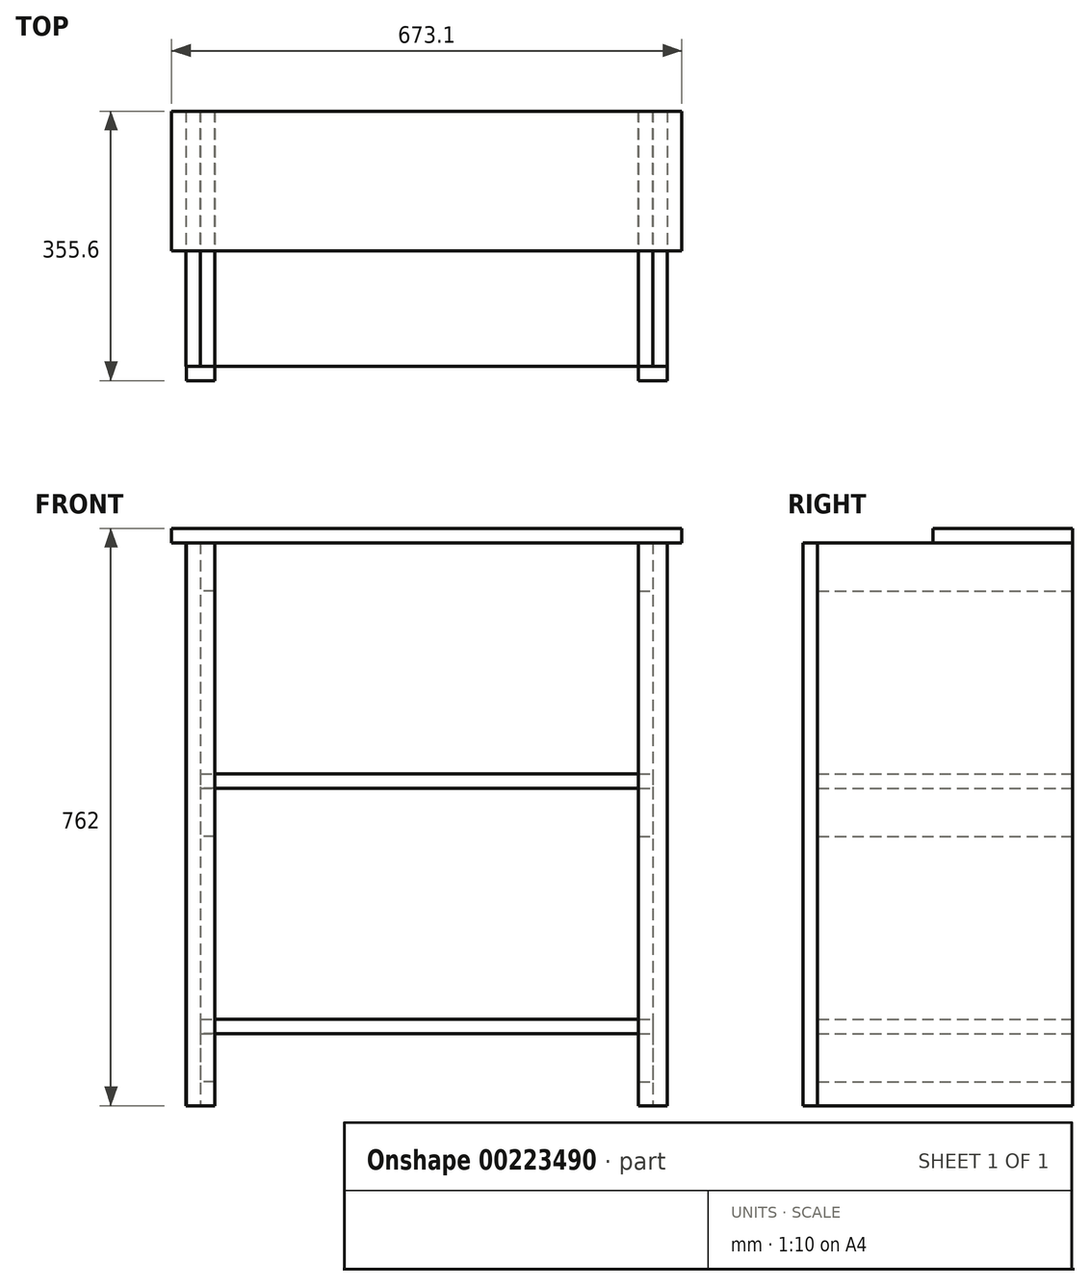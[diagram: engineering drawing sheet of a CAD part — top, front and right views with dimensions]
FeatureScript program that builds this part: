
annotation { "Feature Type Name" : "Feature", "Feature Type Description" : "" }
export const myFeature = defineFeature(function(context is Context, id is Id, definition is map)
    precondition{}
    {
        {
            var Q0;
            Q0=qCreatedBy(makeId("Top.planeOp"),FACE);
            var sketch = newSketch(context, id + "F0", { "sketchPlane" : qUnion([Q0])});
            skLineSegment(sketch, "E0.bottom", {"start": v(-59.58, 81.02) * mm, "end": v(-40.53, 81.02) * mm});
            skLineSegment(sketch, "E0.top", {"start": v(-59.58, 17.52) * mm, "end": v(-40.53, 17.52) * mm});
            skLineSegment(sketch, "E0.left", {"start": v(-59.58, 81.02) * mm, "end": v(-59.58, 17.52) * mm});
            skLineSegment(sketch, "E0.right", {"start": v(-40.53, 81.02) * mm, "end": v(-40.53, 17.52) * mm});
            skLineSegment(sketch, "E1.bottom", {"start": v(-59.58, -192.03) * mm, "end": v(-40.53, -192.03) * mm});
            skLineSegment(sketch, "E1.top", {"start": v(-59.58, -255.53) * mm, "end": v(-40.53, -255.53) * mm});
            skLineSegment(sketch, "E1.left", {"start": v(-59.58, -192.03) * mm, "end": v(-59.58, -255.53) * mm});
            skLineSegment(sketch, "E1.right", {"start": v(-40.53, -192.03) * mm, "end": v(-40.53, -255.53) * mm});
            skLineSegment(sketch, "E2", {"start": v(257.92, 81.02) * mm, "end": v(257.92, -255.53) * mm});
            skLineSegment(sketch, "E3.MirrorCS", {"start": v(575.42, -192.03) * mm, "end": v(575.42, -255.53) * mm});
            skLineSegment(sketch, "E4.MirrorCS", {"start": v(556.37, -192.03) * mm, "end": v(556.37, -255.53) * mm});
            skLineSegment(sketch, "E5.MirrorCS", {"start": v(575.42, -192.03) * mm, "end": v(556.37, -192.03) * mm});
            skLineSegment(sketch, "E6.MirrorCS", {"start": v(575.42, -255.53) * mm, "end": v(556.37, -255.53) * mm});
            skLineSegment(sketch, "E7.MirrorCS", {"start": v(575.42, 17.52) * mm, "end": v(556.37, 17.52) * mm});
            skLineSegment(sketch, "E8.MirrorCS", {"start": v(575.42, 81.02) * mm, "end": v(575.42, 17.52) * mm});
            skLineSegment(sketch, "E9.MirrorCS", {"start": v(556.37, 81.02) * mm, "end": v(556.37, 17.52) * mm});
            skLineSegment(sketch, "E10.MirrorCS", {"start": v(575.42, 81.02) * mm, "end": v(556.37, 81.02) * mm});
            skSolve(sketch);
        }
        {
            var Q0;
            Q0=makeQuery(id+"F0.imprint","IMPRINT",FACE,{"disambiguationData":[TD([[makeQuery(id+"F0.imprint","IMPRINT",EDGE,{"derivedFrom":sQuery(id+"F0.wireOp",EDGE,"E0.bottom")}),-1.0]])]});
            var Q1;
            Q1=makeQuery(id+"F0.imprint","IMPRINT",FACE,{"disambiguationData":[TD([[makeQuery(id+"F0.imprint","IMPRINT",EDGE,{"derivedFrom":sQuery(id+"F0.wireOp",EDGE,"E1.bottom")}),-1.0]])]});
            var Q2;
            Q2=makeQuery(id+"F0.imprint","IMPRINT",FACE,{"disambiguationData":[TD([[makeQuery(id+"F0.imprint","IMPRINT",EDGE,{"derivedFrom":sQuery(id+"F0.wireOp",EDGE,"E3.MirrorCS")}),-1.0]])]});
            var Q3;
            Q3=makeQuery(id+"F0.imprint","IMPRINT",FACE,{"disambiguationData":[TD([[makeQuery(id+"F0.imprint","IMPRINT",EDGE,{"derivedFrom":sQuery(id+"F0.wireOp",EDGE,"E7.MirrorCS")}),-1.0]])]});
            extrude(context, id + "F1", {"entities" : qUnion([Q0, Q1, Q2, Q3]), "depth" : 742.95 * mm});
        }
        {
            var Q0;
            Q0=makeQuery(id+"F1.opExtrude","CAP_FACE",FACE,{"disambiguationData":[OSD([sQuery(id+"F0.wireOp",EDGE,"E7.MirrorCS"),sQuery(id+"F0.wireOp",EDGE,"E8.MirrorCS"),sQuery(id+"F0.wireOp",EDGE,"E9.MirrorCS"),sQuery(id+"F0.wireOp",EDGE,"E10.MirrorCS")])],"isStart":false});
            var sketch = newSketch(context, id + "F2", { "sketchPlane" : qUnion([Q0])});
            skLineSegment(sketch, "E11.bottom", {"start": v(594.47, 81.02) * mm, "end": v(-78.63, 81.02) * mm});
            skLineSegment(sketch, "E11.top", {"start": v(594.47, -103.13) * mm, "end": v(-78.63, -103.13) * mm});
            skLineSegment(sketch, "E11.left", {"start": v(594.47, 81.02) * mm, "end": v(594.47, -103.13) * mm});
            skLineSegment(sketch, "E11.right", {"start": v(-78.63, 81.02) * mm, "end": v(-78.63, -103.13) * mm});
            skLineSegment(sketch, "E12.bottom", {"start": v(-78.63, -103.13) * mm, "end": v(594.47, -103.13) * mm});
            skLineSegment(sketch, "E12.top", {"start": v(-78.63, -282.2) * mm, "end": v(594.47, -282.2) * mm});
            skLineSegment(sketch, "E12.left", {"start": v(-78.63, -103.13) * mm, "end": v(-78.63, -282.2) * mm});
            skLineSegment(sketch, "E12.right", {"start": v(594.47, -103.13) * mm, "end": v(594.47, -282.2) * mm});
            skSolve(sketch);
        }
        {
            var Q0;
            Q0=makeQuery(id+"F2.imprint","IMPRINT",FACE,{"disambiguationData":[TD([[makeQuery(id+"F2.imprint","IMPRINT",EDGE,{"derivedFrom":makeQuery(id+"F1.opExtrude","CAP_EDGE",EDGE,{"disambiguationData":[OSD([sQuery(id+"F0.wireOp",EDGE,"E7.MirrorCS")])],"isStart":false})}),-1.0]])]});
            var Q1;
            {var subQ2=sQuery(id+"F2.wireOp",EDGE,"E11.left");Q1=makeQuery(id+"F2.imprint","IMPRINT",FACE,{"disambiguationData":[TD([[makeQuery(id+"F2.imprint","IMPRINT",EDGE,{"derivedFrom":subQ2}),-1.0]])]});}
            var Q2;
            Q2=makeQuery(id+"F2.imprint","IMPRINT",FACE,{"disambiguationData":[TD([[makeQuery(id+"F2.imprint","IMPRINT",EDGE,{"derivedFrom":sQuery(id+"F2.wireOp",EDGE,"E12.bottom")}),-1.0]])]});
            extrude(context, id + "F3", {"entities" : qUnion([Q0, Q1, Q2]), "depth" : 19.05 * mm});
        }
        {
            var Q0;
            Q0=makeQuery(id+"F1.opExtrude","SWEPT_FACE",FACE,{"disambiguationData":[OSD([sQuery(id+"F0.wireOp",EDGE,"E1.right")])]});
            var sketch = newSketch(context, id + "F4", { "sketchPlane" : qUnion([Q0])});
            skLineSegment(sketch, "E13.bottom", {"start": v(-255.53, 742.95) * mm, "end": v(81.02, 742.95) * mm});
            skLineSegment(sketch, "E13.top", {"start": v(-255.53, 679.45) * mm, "end": v(81.02, 679.45) * mm});
            skLineSegment(sketch, "E13.left", {"start": v(-255.53, 742.95) * mm, "end": v(-255.53, 679.45) * mm});
            skLineSegment(sketch, "E13.right", {"start": v(81.02, 742.95) * mm, "end": v(81.02, 679.45) * mm});
            skLineSegment(sketch, "E14.bottom", {"start": v(-255.53, 419.1) * mm, "end": v(81.02, 419.1) * mm});
            skLineSegment(sketch, "E14.top", {"start": v(-255.53, 355.6) * mm, "end": v(81.02, 355.6) * mm});
            skLineSegment(sketch, "E14.left", {"start": v(-255.53, 419.1) * mm, "end": v(-255.53, 355.6) * mm});
            skLineSegment(sketch, "E14.right", {"start": v(81.02, 419.1) * mm, "end": v(81.02, 355.6) * mm});
            skLineSegment(sketch, "E15.bottom", {"start": v(-255.53, 31.75) * mm, "end": v(81.02, 31.75) * mm});
            skLineSegment(sketch, "E15.top", {"start": v(-255.53, 95.25) * mm, "end": v(81.02, 95.25) * mm});
            skLineSegment(sketch, "E15.left", {"start": v(-255.53, 31.75) * mm, "end": v(-255.53, 95.25) * mm});
            skLineSegment(sketch, "E15.right", {"start": v(81.02, 31.75) * mm, "end": v(81.02, 95.25) * mm});
            skSolve(sketch);
        }
        {
            var Q0;
            {var subQ4=sQuery(id+"F4.wireOp",EDGE,"E13.left");Q0=makeQuery(id+"F4.imprint","IMPRINT",FACE,{"disambiguationData":[TD([[makeQuery(id+"F4.imprint","IMPRINT",EDGE,{"derivedFrom":subQ4}),1.0]])]});}
            var Q1;
            {var subQ3=sQuery(id+"F4.wireOp",EDGE,"E13.right");Q1=makeQuery(id+"F4.imprint","IMPRINT",FACE,{"disambiguationData":[TD([[makeQuery(id+"F4.imprint","IMPRINT",EDGE,{"derivedFrom":subQ3}),-1.0]])]});}
            var Q2;
            {var subQ0=sQuery(id+"F4.wireOp",EDGE,"E14.left");Q2=makeQuery(id+"F4.imprint","IMPRINT",FACE,{"disambiguationData":[TD([[makeQuery(id+"F4.imprint","IMPRINT",EDGE,{"derivedFrom":subQ0}),1.0]])]});}
            var Q3;
            {var subQ0=sQuery(id+"F4.wireOp",EDGE,"E14.right");Q3=makeQuery(id+"F4.imprint","IMPRINT",FACE,{"disambiguationData":[TD([[makeQuery(id+"F4.imprint","IMPRINT",EDGE,{"derivedFrom":subQ0}),-1.0]])]});}
            var Q4;
            {var subQ0=sQuery(id+"F4.wireOp",EDGE,"E15.left");Q4=makeQuery(id+"F4.imprint","IMPRINT",FACE,{"disambiguationData":[TD([[makeQuery(id+"F4.imprint","IMPRINT",EDGE,{"derivedFrom":subQ0}),1.0]])]});}
            var Q5;
            {var subQ0=sQuery(id+"F4.wireOp",EDGE,"E15.right");Q5=makeQuery(id+"F4.imprint","IMPRINT",FACE,{"disambiguationData":[TD([[makeQuery(id+"F4.imprint","IMPRINT",EDGE,{"derivedFrom":subQ0}),1.0]])]});}
            extrude(context, id + "F5", {"entities" : qUnion([Q0, Q1, Q2, Q3, Q4, Q5]), "depth" : 19.05 * mm});
        }
        {
            var Q0;
            Q0=makeQuery(id+"F1.opExtrude","SWEPT_FACE",FACE,{"disambiguationData":[OSD([sQuery(id+"F0.wireOp",EDGE,"E9.MirrorCS")])]});
            cPlane(context, id + "F6", {"entities" : qUnion([Q0]), "cplaneType" : CPlaneType.OFFSET, "offset" : 298.45 * mm, "width" : 152.4 * mm, "height" : 152.4 * mm});
        }
        {
            var Q0;
            Q0=makeQuery(id+"F5.opExtrude","SWEPT_BODY",BODY,{"disambiguationData":[OSD([sQuery(id+"F4.wireOp",EDGE,"E15.bottom"),sQuery(id+"F4.wireOp",EDGE,"E15.top"),sQuery(id+"F4.wireOp",EDGE,"E15.left"),sQuery(id+"F4.wireOp",EDGE,"E15.right")])]});
            var Q1;
            Q1=makeQuery(id+"F5.opExtrude","SWEPT_BODY",BODY,{"disambiguationData":[OSD([sQuery(id+"F4.wireOp",EDGE,"E14.bottom"),sQuery(id+"F4.wireOp",EDGE,"E14.top"),sQuery(id+"F4.wireOp",EDGE,"E14.left"),sQuery(id+"F4.wireOp",EDGE,"E14.right")])]});
            var Q2;
            Q2=makeQuery(id+"F5.opExtrude","SWEPT_BODY",BODY,{"disambiguationData":[OSD([sQuery(id+"F4.wireOp",EDGE,"E13.bottom"),sQuery(id+"F4.wireOp",EDGE,"E13.top"),sQuery(id+"F4.wireOp",EDGE,"E13.left"),sQuery(id+"F4.wireOp",EDGE,"E13.right")])]});
            var Q3;
            Q3=qCreatedBy(id+"F6.planeOp",FACE);
            mirror(context, id + "F7", {"entities" : qUnion([Q0, Q1, Q2]), "mirrorPlane" : qUnion([Q3])});
        }
        {
            var Q0;
            Q0=makeQuery(id+"F5.opExtrude","SWEPT_FACE",FACE,{"disambiguationData":[OSD([sQuery(id+"F4.wireOp",EDGE,"E15.top")])]});
            var sketch = newSketch(context, id + "F8", { "sketchPlane" : qUnion([Q0])});
            skPoint(sketch, "E16.oppositeSnap0", {"position": v(-31, -255.53) * mm});
            skLineSegment(sketch, "E16.bottom", {"start": v(-40.53, 81.02) * mm, "end": v(556.37, 81.02) * mm});
            skLineSegment(sketch, "E16.top", {"start": v(-40.53, -255.53) * mm, "end": v(556.37, -255.53) * mm});
            skLineSegment(sketch, "E16.left", {"start": v(-40.53, 81.02) * mm, "end": v(-40.53, -255.53) * mm});
            skLineSegment(sketch, "E16.right", {"start": v(556.37, 81.02) * mm, "end": v(556.37, -255.53) * mm});
            skLineSegment(sketch, "E17.bottom", {"start": v(-21.48, -255.53) * mm, "end": v(537.32, -255.53) * mm});
            skLineSegment(sketch, "E17.top", {"start": v(-21.48, -274.58) * mm, "end": v(537.32, -274.58) * mm});
            skLineSegment(sketch, "E17.left", {"start": v(-21.48, -255.53) * mm, "end": v(-21.48, -274.58) * mm});
            skLineSegment(sketch, "E17.right", {"start": v(537.32, -255.53) * mm, "end": v(537.32, -274.58) * mm});
            skSolve(sketch);
        }
        {
            var Q0;
            {var subQ2=sQuery(id+"F8.wireOp",EDGE,"E16.right");Q0=makeQuery(id+"F8.imprint","IMPRINT",FACE,{"disambiguationData":[TD([[makeQuery(id+"F8.imprint","IMPRINT",EDGE,{"derivedFrom":subQ2}),-1.0]])]});}
            var Q1;
            {var subQ0=sQuery(id+"F8.wireOp",EDGE,"E16.left");Q1=makeQuery(id+"F8.imprint","IMPRINT",FACE,{"disambiguationData":[TD([[makeQuery(id+"F8.imprint","IMPRINT",EDGE,{"derivedFrom":subQ0}),-1.0]])]});}
            var Q2;
            Q2=makeQuery(id+"F8.imprint","IMPRINT",FACE,{"disambiguationData":[TD([[makeQuery(id+"F8.imprint","IMPRINT",EDGE,{"derivedFrom":sQuery(id+"F8.wireOp",EDGE,"E17.bottom")}),-1.0]])]});
            extrude(context, id + "F9", {"entities" : qUnion([Q0, Q1, Q2]), "depth" : 19.05 * mm});
        }
        {
            var Q0;
            Q0=makeQuery(id+"F5.opExtrude","SWEPT_FACE",FACE,{"disambiguationData":[OSD([sQuery(id+"F4.wireOp",EDGE,"E14.bottom")])]});
            var sketch = newSketch(context, id + "F10", { "sketchPlane" : qUnion([Q0])});
            skLineSegment(sketch, "E18.bottom", {"start": v(-40.53, 81.02) * mm, "end": v(556.37, 81.02) * mm});
            skLineSegment(sketch, "E18.top", {"start": v(-40.53, -255.53) * mm, "end": v(556.37, -255.53) * mm});
            skLineSegment(sketch, "E18.left", {"start": v(-40.53, 81.02) * mm, "end": v(-40.53, -255.53) * mm});
            skLineSegment(sketch, "E18.right", {"start": v(556.37, 81.02) * mm, "end": v(556.37, -255.53) * mm});
            skLineSegment(sketch, "E19.bottom", {"start": v(-21.48, -255.53) * mm, "end": v(537.32, -255.53) * mm});
            skLineSegment(sketch, "E19.top", {"start": v(-21.48, -274.58) * mm, "end": v(537.32, -274.58) * mm});
            skLineSegment(sketch, "E19.left", {"start": v(-21.48, -255.53) * mm, "end": v(-21.48, -274.58) * mm});
            skLineSegment(sketch, "E19.right", {"start": v(537.32, -255.53) * mm, "end": v(537.32, -274.58) * mm});
            skSolve(sketch);
        }
        {
            var Q0;
            {var subQ2=sQuery(id+"F10.wireOp",EDGE,"E18.right");Q0=makeQuery(id+"F10.imprint","IMPRINT",FACE,{"disambiguationData":[TD([[makeQuery(id+"F10.imprint","IMPRINT",EDGE,{"derivedFrom":subQ2}),-1.0]])]});}
            var Q1;
            {var subQ0=sQuery(id+"F10.wireOp",EDGE,"E18.left");Q1=makeQuery(id+"F10.imprint","IMPRINT",FACE,{"disambiguationData":[TD([[makeQuery(id+"F10.imprint","IMPRINT",EDGE,{"derivedFrom":subQ0}),-1.0]])]});}
            var Q2;
            Q2=makeQuery(id+"F10.imprint","IMPRINT",FACE,{"disambiguationData":[TD([[makeQuery(id+"F10.imprint","IMPRINT",EDGE,{"derivedFrom":sQuery(id+"F10.wireOp",EDGE,"E19.bottom")}),-1.0]])]});
            extrude(context, id + "F11", {"entities" : qUnion([Q0, Q1, Q2]), "depth" : 19.05 * mm});
        }
        {
            var Q0;
            Q0=makeQuery(id+"F1.opExtrude","SWEPT_BODY",BODY,{"disambiguationData":[OSD([sQuery(id+"F0.wireOp",EDGE,"E3.MirrorCS"),sQuery(id+"F0.wireOp",EDGE,"E4.MirrorCS"),sQuery(id+"F0.wireOp",EDGE,"E5.MirrorCS"),sQuery(id+"F0.wireOp",EDGE,"E6.MirrorCS")])]});
            deleteBodies(context, id + "F12", {"entities" : qUnion([Q0])});
        }
        {
            var Q0;
            Q0=makeQuery(id+"F1.opExtrude","SWEPT_BODY",BODY,{"disambiguationData":[OSD([sQuery(id+"F0.wireOp",EDGE,"E7.MirrorCS"),sQuery(id+"F0.wireOp",EDGE,"E8.MirrorCS"),sQuery(id+"F0.wireOp",EDGE,"E9.MirrorCS"),sQuery(id+"F0.wireOp",EDGE,"E10.MirrorCS")])]});
            deleteBodies(context, id + "F13", {"entities" : qUnion([Q0])});
        }
        {
            var Q0;
            Q0=makeQuery(id+"F1.opExtrude","SWEPT_BODY",BODY,{"disambiguationData":[OSD([sQuery(id+"F0.wireOp",EDGE,"E1.bottom"),sQuery(id+"F0.wireOp",EDGE,"E1.top"),sQuery(id+"F0.wireOp",EDGE,"E1.left"),sQuery(id+"F0.wireOp",EDGE,"E1.right")])]});
            deleteBodies(context, id + "F14", {"entities" : qUnion([Q0])});
        }
        {
            var Q0;
            Q0=makeQuery(id+"F1.opExtrude","SWEPT_BODY",BODY,{"disambiguationData":[OSD([sQuery(id+"F0.wireOp",EDGE,"E0.bottom"),sQuery(id+"F0.wireOp",EDGE,"E0.top"),sQuery(id+"F0.wireOp",EDGE,"E0.left"),sQuery(id+"F0.wireOp",EDGE,"E0.right")])]});
            deleteBodies(context, id + "F15", {"entities" : qUnion([Q0])});
        }
        {
            var Q0;
            Q0=makeQuery(id+"F7.opPattern","COPY",FACE,{"derivedFrom":makeQuery(id+"F5.opExtrude","CAP_FACE",FACE,{"disambiguationData":[OSD([sQuery(id+"F4.wireOp",EDGE,"E13.bottom"),sQuery(id+"F4.wireOp",EDGE,"E13.top"),sQuery(id+"F4.wireOp",EDGE,"E13.left"),sQuery(id+"F4.wireOp",EDGE,"E13.right")])],"isStart":true}),"instanceName":"1"});
            var sketch = newSketch(context, id + "F16", { "sketchPlane" : qUnion([Q0])});
            skLineSegment(sketch, "E20.bottom", {"start": v(81.02, 742.95) * mm, "end": v(-255.53, 742.95) * mm});
            skLineSegment(sketch, "E20.top", {"start": v(81.02, 0) * mm, "end": v(-255.53, 0) * mm});
            skLineSegment(sketch, "E20.left", {"start": v(81.02, 742.95) * mm, "end": v(81.02, 0) * mm});
            skLineSegment(sketch, "E20.right", {"start": v(-255.53, 742.95) * mm, "end": v(-255.53, 0) * mm});
            skSolve(sketch);
        }
        {
            var Q0;
            {var subQ0=sQuery(id+"F16.wireOp",EDGE,"E20.top");Q0=makeQuery(id+"F16.imprint","IMPRINT",FACE,{"disambiguationData":[TD([[makeQuery(id+"F16.imprint","IMPRINT",EDGE,{"derivedFrom":subQ0}),-1.0]])]});}
            var Q1;
            {var subQ0=sQuery(id+"F16.wireOp",EDGE,"E20.bottom");Q1=makeQuery(id+"F16.imprint","IMPRINT",FACE,{"disambiguationData":[TD([[makeQuery(id+"F16.imprint","IMPRINT",EDGE,{"derivedFrom":subQ0}),1.0]])]});}
            extrude(context, id + "F17", {"entities" : qUnion([Q0, Q1]), "depth" : 19.05 * mm});
        }
        {
            var Q0;
            Q0=makeQuery(id+"F17.opExtrude","SWEPT_BODY",BODY,{"disambiguationData":[OSD([sQuery(id+"F16.wireOp",EDGE,"E20.bottom"),sQuery(id+"F16.wireOp",EDGE,"E20.top"),sQuery(id+"F16.wireOp",EDGE,"E20.left"),sQuery(id+"F16.wireOp",EDGE,"E20.right")])]});
            var Q1;
            Q1=qCreatedBy(id+"F6.planeOp",FACE);
            mirror(context, id + "F18", {"entities" : qUnion([Q0]), "mirrorPlane" : qUnion([Q1])});
        }
        {
            var Q0;
            Q0=makeQuery(id+"F18.opPattern","COPY",FACE,{"derivedFrom":makeQuery(id+"F17.opExtrude","SWEPT_FACE",FACE,{"disambiguationData":[OSD([sQuery(id+"F16.wireOp",EDGE,"E20.right")])]}),"instanceName":"1"});
            var sketch = newSketch(context, id + "F19", { "sketchPlane" : qUnion([Q0])});
            skSolve(sketch);
        }
        {
            var Q0;
            {var subQ0=sQuery(id+"F16.wireOp",EDGE,"E20.right");Q0=makeQuery(id+"F19.imprint","IMPRINT",FACE,{"disambiguationData":[TD([[makeQuery(id+"F19.imprint","IMPRINT",EDGE,{"derivedFrom":makeQuery(id+"F18.opPattern","COPY",EDGE,{"derivedFrom":makeQuery(id+"F17.opExtrude","CAP_EDGE",EDGE,{"disambiguationData":[OSD([subQ0])],"isStart":true}),"instanceName":"1"})}),-1.0]])]});}
            var sketch = newSketch(context, id + "F20", { "sketchPlane" : qUnion([Q0])});
            skLineSegment(sketch, "E21.bottom", {"start": v(-59.42, 742.95) * mm, "end": v(-21.32, 742.95) * mm});
            skLineSegment(sketch, "E21.top", {"start": v(-59.42, 0) * mm, "end": v(-21.32, 0) * mm});
            skLineSegment(sketch, "E21.left", {"start": v(-59.42, 742.95) * mm, "end": v(-59.42, 0) * mm});
            skLineSegment(sketch, "E21.right", {"start": v(-21.32, 742.95) * mm, "end": v(-21.32, 0) * mm});
            skSolve(sketch);
        }
        {
            var Q0;
            {var subQ2=sQuery(id+"F20.wireOp",EDGE,"E21.right");Q0=makeQuery(id+"F20.imprint","IMPRINT",FACE,{"disambiguationData":[TD([[makeQuery(id+"F20.imprint","IMPRINT",EDGE,{"derivedFrom":subQ2}),-1.0]])]});}
            var Q1;
            {var subQ3=sQuery(id+"F20.wireOp",EDGE,"E21.left");Q1=makeQuery(id+"F20.imprint","IMPRINT",FACE,{"disambiguationData":[TD([[makeQuery(id+"F20.imprint","IMPRINT",EDGE,{"derivedFrom":subQ3}),1.0]])]});}
            extrude(context, id + "F21", {"entities" : qUnion([Q0, Q1]), "depth" : 19.05 * mm});
        }
        {
            var Q0;
            Q0=makeQuery(id+"F21.opExtrude","SWEPT_BODY",BODY,{"disambiguationData":[OSD([sQuery(id+"F20.wireOp",EDGE,"E21.bottom"),sQuery(id+"F20.wireOp",EDGE,"E21.top"),sQuery(id+"F20.wireOp",EDGE,"E21.left"),sQuery(id+"F20.wireOp",EDGE,"E21.right")])]});
            var Q1;
            Q1=qCreatedBy(id+"F6.planeOp",FACE);
            mirror(context, id + "F22", {"entities" : qUnion([Q0]), "mirrorPlane" : qUnion([Q1])});
        }
    });
